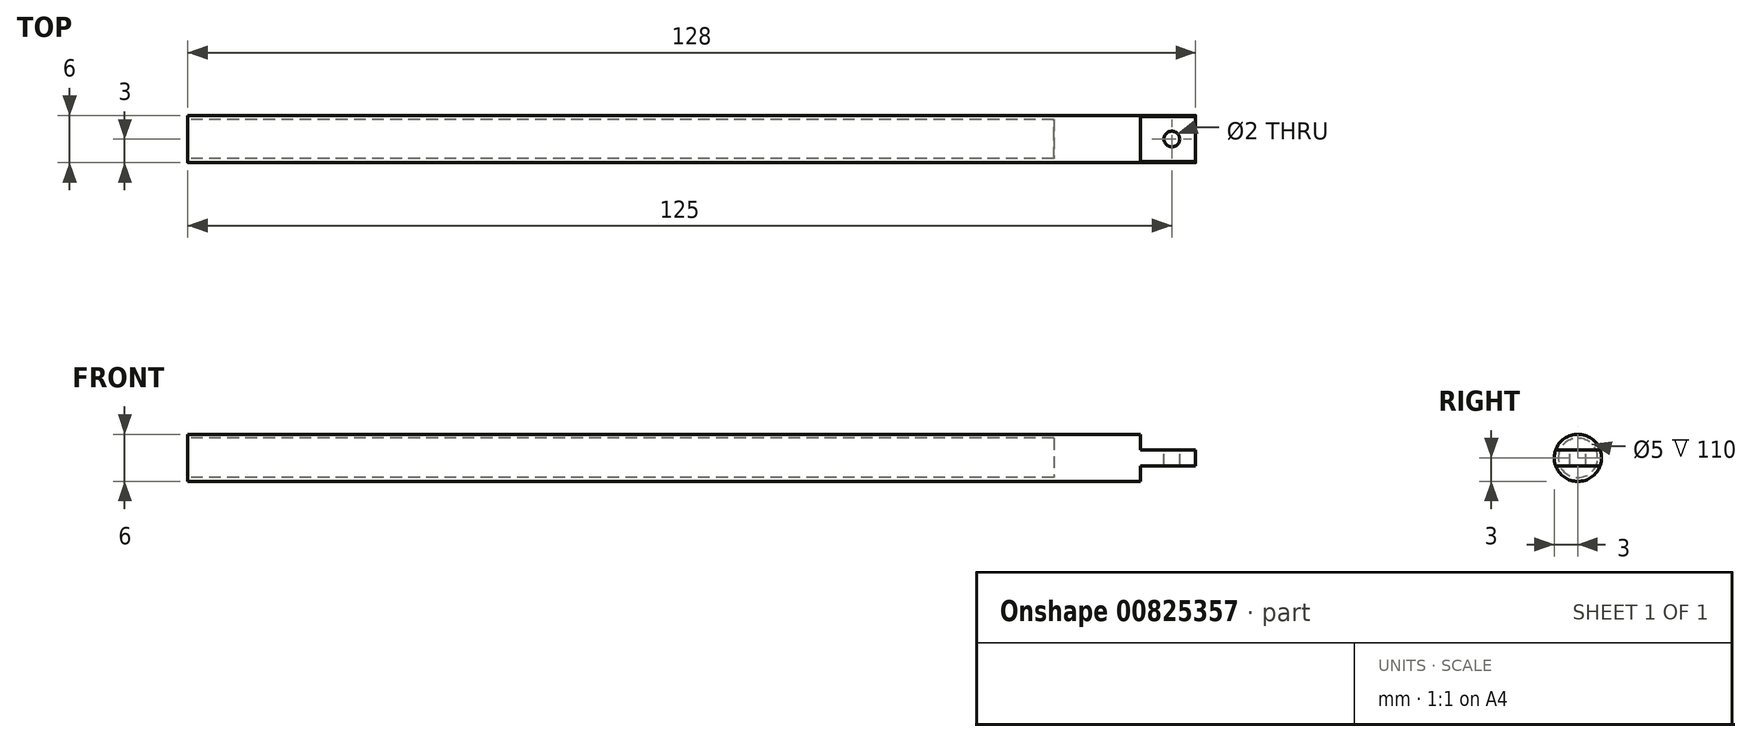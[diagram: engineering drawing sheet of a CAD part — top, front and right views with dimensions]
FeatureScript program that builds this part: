
annotation { "Feature Type Name" : "Feature", "Feature Type Description" : "" }
export const myFeature = defineFeature(function(context is Context, id is Id, definition is map)
    precondition{}
    {
        {
            var Q0;
            Q0=qCreatedBy(makeId("Right.planeOp"),FACE);
            var sketch = newSketch(context, id + "F0", { "sketchPlane" : qUnion([Q0])});
            skCircle(sketch, "E0", {"center": v(0, 0) * mm, "radius": 3 * mm});
            skSolve(sketch);
        }
        {
            var Q0;
            Q0 = qSketchRegion(id + "F0", true);
            extrude(context, id + "F1", {"entities" : qUnion([Q0]), "depth" : 128 * mm, "offsetDistance" : 25 * mm});
        }
        {
            var Q0;
            Q0=makeQuery(id+"F1.opExtrude","CAP_FACE",FACE,{"disambiguationData":[OSD([sQuery(id+"F0.wireOp",EDGE,"E0")])],"isStart":false});
            var sketch = newSketch(context, id + "F2", { "sketchPlane" : qUnion([Q0])});
            skLineSegment(sketch, "E1.bottom", {"start": v(5, 1) * mm, "end": v(-5, 1) * mm});
            skLineSegment(sketch, "E1.top", {"start": v(5, 4.73) * mm, "end": v(-5, 4.73) * mm});
            skLineSegment(sketch, "E1.left", {"start": v(5, 1) * mm, "end": v(5, 4.73) * mm});
            skLineSegment(sketch, "E1.right", {"start": v(-5, 1) * mm, "end": v(-5, 4.73) * mm});
            skPoint(sketch, "E1.middle", {"position": v(0, 2.86) * mm});
            skSolve(sketch);
        }
        {
            var Q0;
            Q0 = qSketchRegion(id + "F2", true);
            extrude(context, id + "F3", {"entities" : qUnion([Q0]), "operationType" : NewBodyOperationType.REMOVE, "oppositeDirection" : true, "depth" : 7 * mm, "offsetDistance" : 25 * mm});
        }
        {
            var Q0;
            Q0=makeQuery(id+"F1.opExtrude","CAP_FACE",FACE,{"disambiguationData":[OSD([sQuery(id+"F0.wireOp",EDGE,"E0")])],"isStart":false});
            var sketch = newSketch(context, id + "F4", { "sketchPlane" : qUnion([Q0])});
            skLineSegment(sketch, "E2.bottom", {"start": v(-5, -1) * mm, "end": v(5, -1) * mm});
            skLineSegment(sketch, "E2.top", {"start": v(-5, -11) * mm, "end": v(5, -11) * mm});
            skLineSegment(sketch, "E2.left", {"start": v(-5, -1) * mm, "end": v(-5, -11) * mm});
            skLineSegment(sketch, "E2.right", {"start": v(5, -1) * mm, "end": v(5, -11) * mm});
            skPoint(sketch, "E2.middle", {"position": v(0, -6) * mm});
            skSolve(sketch);
        }
        {
            var Q0;
            Q0 = qSketchRegion(id + "F4", true);
            extrude(context, id + "F5", {"entities" : qUnion([Q0]), "operationType" : NewBodyOperationType.REMOVE, "oppositeDirection" : true, "depth" : 7 * mm, "offsetDistance" : 25 * mm});
        }
        {
            var Q0;
            Q0=makeQuery(id+"F3.boolean.opBoolean","COPY",FACE,{"derivedFrom":makeQuery(id+"F3.opExtrude","SWEPT_FACE",FACE,{"disambiguationData":[OSD([sQuery(id+"F2.wireOp",EDGE,"E1.bottom")])]})});
            var sketch = newSketch(context, id + "F6", { "sketchPlane" : qUnion([Q0])});
            skCircle(sketch, "E3", {"center": v(125, 0) * mm, "radius": 1 * mm});
            skSolve(sketch);
        }
        {
            var Q0;
            Q0=makeQuery(id+"F6.imprint","IMPRINT",FACE,{"disambiguationData":[TD([[makeQuery(id+"F6.imprint","IMPRINT",EDGE,{"derivedFrom":sQuery(id+"F6.wireOp",EDGE,"E3")}),1.0]])]});
            extrude(context, id + "F7", {"entities" : qUnion([Q0]), "operationType" : NewBodyOperationType.REMOVE, "oppositeDirection" : true, "depth" : 10 * mm, "offsetDistance" : 25 * mm});
        }
        {
            var Q0;
            Q0=makeQuery(id+"F1.opExtrude","CAP_FACE",FACE,{"disambiguationData":[OSD([sQuery(id+"F0.wireOp",EDGE,"E0")])],"isStart":true});
            var sketch = newSketch(context, id + "F8", { "sketchPlane" : qUnion([Q0])});
            skCircle(sketch, "E4", {"center": v(0, 0) * mm, "radius": 2.5 * mm});
            skSolve(sketch);
        }
        {
            var Q0;
            Q0 = qSketchRegion(id + "F8", true);
            extrude(context, id + "F9", {"entities" : qUnion([Q0]), "operationType" : NewBodyOperationType.REMOVE, "oppositeDirection" : true, "depth" : 110 * mm, "offsetDistance" : 25 * mm});
        }
    });
